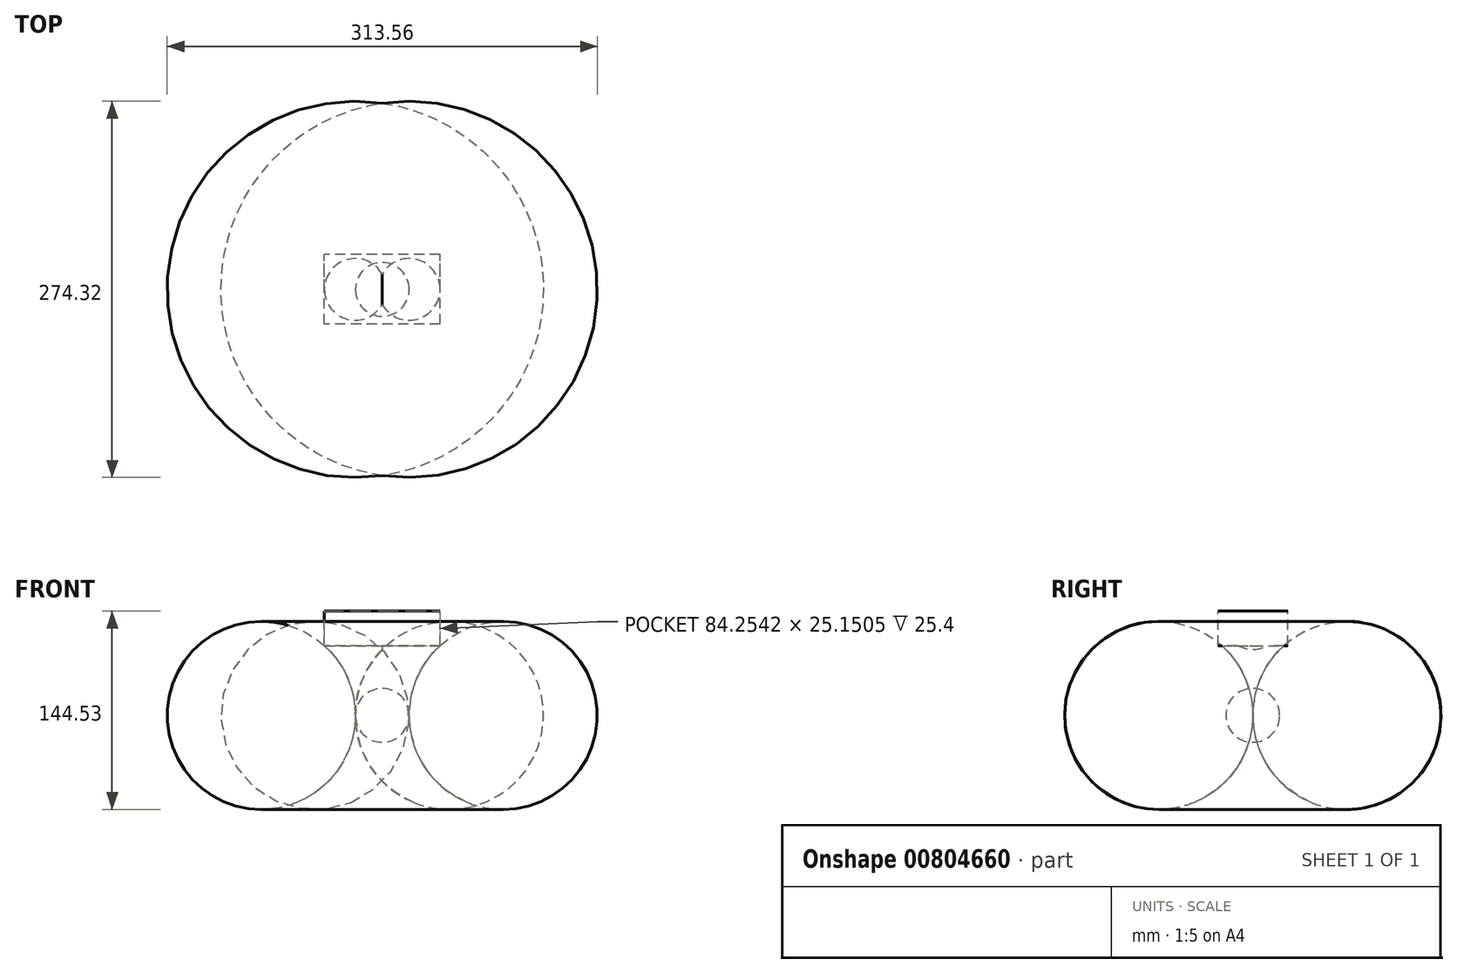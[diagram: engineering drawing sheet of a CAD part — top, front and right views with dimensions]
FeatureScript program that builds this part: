
annotation { "Feature Type Name" : "Feature", "Feature Type Description" : "" }
export const myFeature = defineFeature(function(context is Context, id is Id, definition is map)
    precondition{}
    {
        {
            var Q0;
            Q0=qCreatedBy(makeId("Front.planeOp"),FACE);
            var sketch = newSketch(context, id + "F0", { "sketchPlane" : qUnion([Q0])});
            skLineSegment(sketch, "E0.bottom", {"start": v(10.22, 9.75) * mm, "end": v(-74.04, 9.75) * mm});
            skLineSegment(sketch, "E0.top", {"start": v(10.22, 34.9) * mm, "end": v(-74.04, 34.9) * mm});
            skLineSegment(sketch, "E0.left", {"start": v(10.22, 9.75) * mm, "end": v(10.22, 34.9) * mm});
            skLineSegment(sketch, "E0.right", {"start": v(-74.04, 9.75) * mm, "end": v(-74.04, 34.9) * mm});
            skPoint(sketch, "E0.middle", {"position": v(-31.9, 22.32) * mm});
            skSolve(sketch);
        }
        {
            var Q0;
            Q0=makeQuery(id+"F0.imprint","IMPRINT",FACE,{"disambiguationData":[TD([[makeQuery(id+"F0.imprint","IMPRINT",EDGE,{"derivedFrom":sQuery(id+"F0.wireOp",EDGE,"E0.bottom")}),-1.0]])]});
            var sketch = newSketch(context, id + "F1", { "sketchPlane" : qUnion([Q0])});
            skCircle(sketch, "E1", {"center": v(-31.9, -41.05) * mm, "radius": 19.62 * mm});
            skLineSegment(sketch, "E2", {"start": v(-51.53, -41.05) * mm, "end": v(-51.53, 9.75) * mm});
            skLineSegment(sketch, "E3", {"start": v(-12.3, -41.05) * mm, "end": v(-12.3, 9.75) * mm});
            skArc(sketch, "E4", {"start": v(10.22, 9.75) * mm, "mid": v(-6.41, -13.27) * mm, "end": v(-12.3, -41.05) * mm});
            skArc(sketch, "E5", {"start": v(-51.53, -41.05) * mm, "mid": v(-57.4, -13.27) * mm, "end": v(-74.04, 9.75) * mm});
            skLineSegment(sketch, "E6", {"start": v(-51.53, -41.05) * mm, "end": v(-12.3, -41.05) * mm});
            skSolve(sketch);
        }
        {
            var Q0;
            Q0=makeQuery(id+"F0.imprint","IMPRINT",FACE,{"disambiguationData":[TD([[makeQuery(id+"F0.imprint","IMPRINT",EDGE,{"derivedFrom":sQuery(id+"F0.wireOp",EDGE,"E0.bottom")}),-1.0]])]});
            extrude(context, id + "F2", {"entities" : qUnion([Q0]), "endBound" : BoundingType.SYMMETRIC, "depth" : 50.8 * mm, "offsetDistance" : 25.4 * mm});
        }
        {
            var Q0;
            {var subQ0=sQuery(id+"F1.wireOp",EDGE,"E3");Q0=makeQuery(id+"F1.imprint","IMPRINT",FACE,{"disambiguationData":[TD([[makeQuery(id+"F1.imprint","IMPRINT",EDGE,{"derivedFrom":subQ0}),-1.0]])]});}
            var Q1;
            Q1=sQuery(id+"F1.wireOp",EDGE,"E3");
            revolve(context, id + "F3", {"operationType" : NewBodyOperationType.ADD, "surfaceOperationType" : NewSurfaceOperationType.NEW, "entities" : qUnion([Q0]), "axis" : qUnion([Q1]), "revolveType" : RevolveType.FULL});
        }
        {
            var Q0;
            {var subQ0=sQuery(id+"F1.wireOp",EDGE,"E2");Q0=makeQuery(id+"F1.imprint","IMPRINT",FACE,{"disambiguationData":[TD([[makeQuery(id+"F1.imprint","IMPRINT",EDGE,{"derivedFrom":subQ0}),1.0]])]});}
            var Q1;
            Q1=sQuery(id+"F1.wireOp",EDGE,"E2");
            revolve(context, id + "F4", {"operationType" : NewBodyOperationType.ADD, "surfaceOperationType" : NewSurfaceOperationType.NEW, "entities" : qUnion([Q0]), "axis" : qUnion([Q1]), "revolveType" : RevolveType.FULL});
        }
        {
            var Q0;
            {var subQ0=sQuery(id+"F1.wireOp",EDGE,"E6");Q0=makeQuery(id+"F1.imprint","IMPRINT",FACE,{"disambiguationData":[TD([[makeQuery(id+"F1.imprint","IMPRINT",EDGE,{"derivedFrom":subQ0}),-1.0]])]});}
            var Q1;
            Q1=sQuery(id+"F1.wireOp",EDGE,"E6");
            revolve(context, id + "F5", {"operationType" : NewBodyOperationType.ADD, "surfaceOperationType" : NewSurfaceOperationType.NEW, "entities" : qUnion([Q0]), "axis" : qUnion([Q1]), "revolveType" : RevolveType.FULL});
        }
    });
